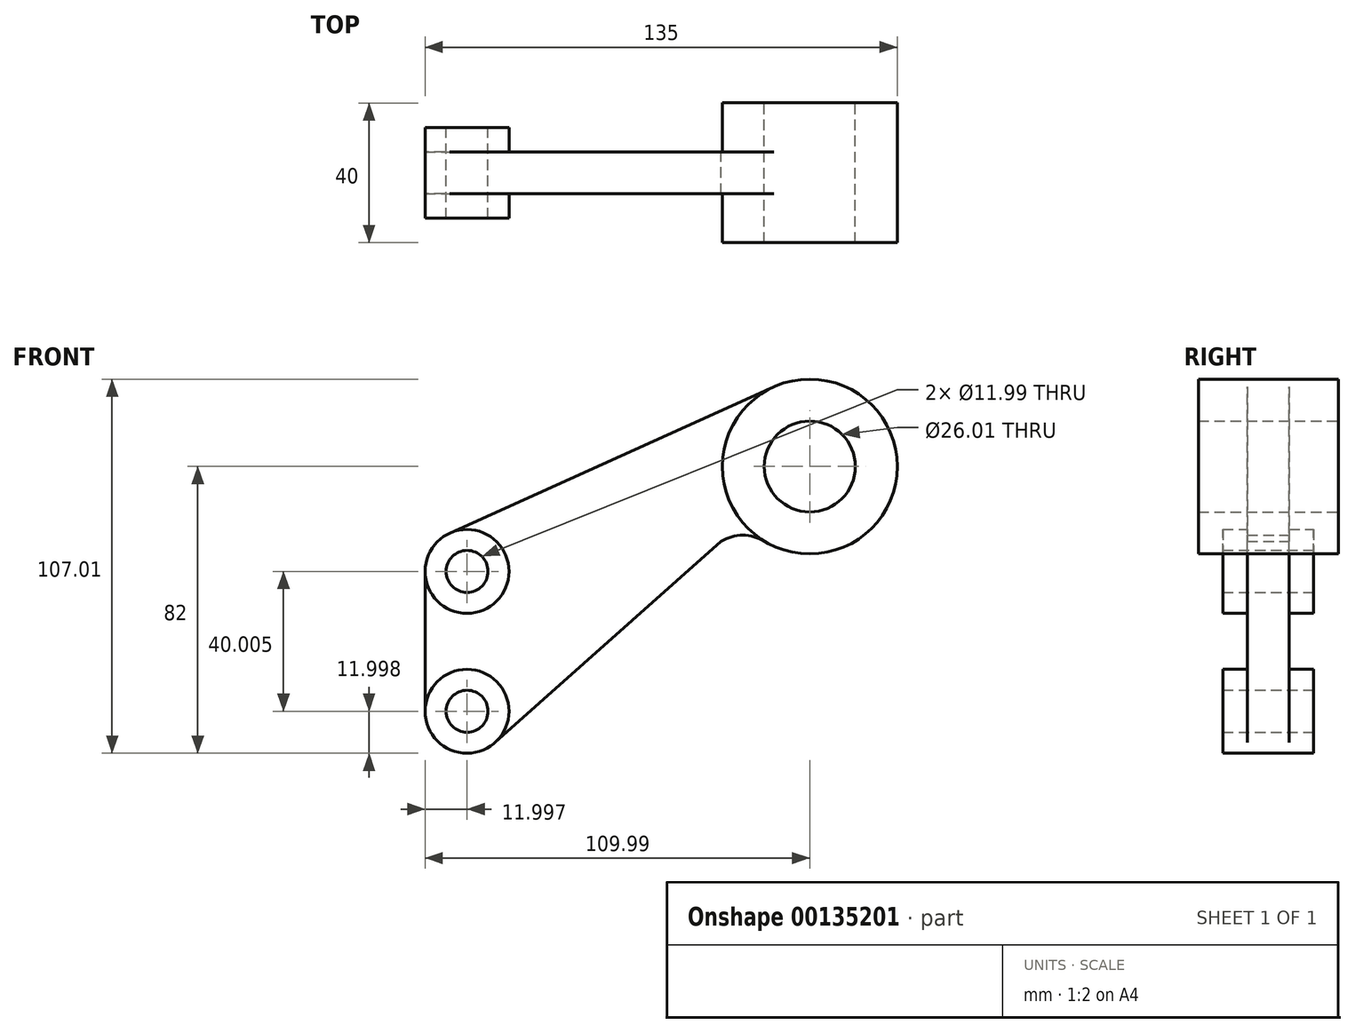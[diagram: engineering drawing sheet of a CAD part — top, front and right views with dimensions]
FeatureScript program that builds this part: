
annotation { "Feature Type Name" : "Feature", "Feature Type Description" : "" }
export const myFeature = defineFeature(function(context is Context, id is Id, definition is map)
    precondition{}
    {
        {
            var Q0;
            Q0=qCreatedBy(makeId("Front.planeOp"),FACE);
            var sketch = newSketch(context, id + "F0", { "sketchPlane" : qUnion([Q0])});
            skCircle(sketch, "E0", {"center": v(0, 0) * mm, "radius": 13 * mm});
            skCircle(sketch, "E1", {"center": v(0, 0) * mm, "radius": 25 * mm});
            skCircle(sketch, "E2", {"center": v(-98, -30) * mm, "radius": 6 * mm});
            skCircle(sketch, "E3", {"center": v(-98, -30) * mm, "radius": 12 * mm});
            skCircle(sketch, "E4", {"center": v(-98, -70) * mm, "radius": 6 * mm});
            skCircle(sketch, "E5", {"center": v(-98, -70) * mm, "radius": 12 * mm});
            skLineSegment(sketch, "E6", {"start": v(-110, -30) * mm, "end": v(-110, -70) * mm});
            skArc(sketch, "E7", {"start": v(-12.95, -21.4) * mm, "mid": v(-19.16, -19.66) * mm, "end": v(-25.37, -21.4) * mm});
            skLineSegment(sketch, "E8", {"start": v(-90.01, -78.96) * mm, "end": v(-25.37, -21.4) * mm});
            skLineSegment(sketch, "E9", {"start": v(-102.93, -19.06) * mm, "end": v(-10.3, 22.79) * mm});
            skSolve(sketch);
        }
        {
            var Q0;
            Q0=makeQuery(id+"F0.imprint","IMPRINT",FACE,{"disambiguationData":[TD([[makeQuery(id+"F0.imprint","IMPRINT",EDGE,{"derivedFrom":sQuery(id+"F0.wireOp",EDGE,"E0")}),-1.0]])]});
            extrude(context, id + "F1", {"entities" : qUnion([Q0]), "endBound" : BoundingType.SYMMETRIC, "depth" : 40 * mm});
        }
        {
            var Q0;
            {var subQ0=sQuery(id+"F0.wireOp",EDGE,"E6");Q0=makeQuery(id+"F0.imprint","IMPRINT",FACE,{"disambiguationData":[TD([[makeQuery(id+"F0.imprint","IMPRINT",EDGE,{"derivedFrom":subQ0}),1.0]])]});}
            extrude(context, id + "F2", {"entities" : qUnion([Q0]), "operationType" : NewBodyOperationType.ADD, "endBound" : BoundingType.SYMMETRIC, "depth" : 12 * mm});
        }
        {
            var Q0;
            Q0=makeQuery(id+"F0.imprint","IMPRINT",FACE,{"disambiguationData":[TD([[makeQuery(id+"F0.imprint","IMPRINT",EDGE,{"derivedFrom":sQuery(id+"F0.wireOp",EDGE,"E2")}),-1.0]])]});
            var Q1;
            Q1=makeQuery(id+"F0.imprint","IMPRINT",FACE,{"disambiguationData":[TD([[makeQuery(id+"F0.imprint","IMPRINT",EDGE,{"derivedFrom":sQuery(id+"F0.wireOp",EDGE,"E4")}),-1.0]])]});
            extrude(context, id + "F3", {"entities" : qUnion([Q0, Q1]), "operationType" : NewBodyOperationType.ADD, "endBound" : BoundingType.SYMMETRIC, "depth" : 26 * mm});
        }
    });
